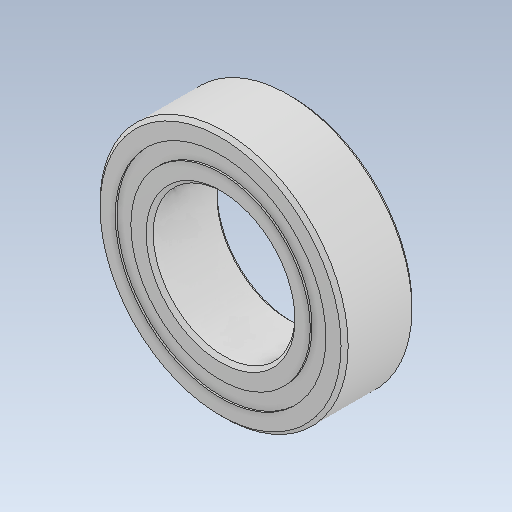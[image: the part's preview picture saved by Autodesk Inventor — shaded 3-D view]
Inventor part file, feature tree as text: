
AUTODESK INVENTOR PART (.ipt)
format: ipt  version: 2020 (Build 240168000, 168)  size: 607,232 bytes
history: native  units: in
note: dims shown in document units (in); Inventor stores cm internally (conversion verified against a paired STEP export)
features: other x11, revolve x5
ambient origin geometry x8: Origin, YZ Plane, XZ Plane, XY Plane, X Axis, Y Axis, Z Axis, Center Point
bodies: Solid1 (feature_tree), Solid2 (feature_tree), Solid3 (feature_tree), Solid4 (feature_tree), Solid5 (feature_tree), Solid6 (feature_tree), Solid7 (feature_tree), Solid8 (feature_tree), Solid9 (feature_tree), Solid10 (feature_tree), Solid11 (feature_tree), Solid12 (feature_tree), Solid13 (feature_tree), Solid14 (feature_tree), Solid15 (feature_tree), Solid16 (feature_tree)
feature tree (16):
  revolve  "Revolve1"  [1 undecoded]
  revolve  "Revolve3"  [1 undecoded]
  revolve  "Revolve4"  [1 undecoded]
  other  "CirPattern1[1]"
  other  "CirPattern1[2]"
  other  "CirPattern1[3]"
  other  "CirPattern1[4]"
  other  "CirPattern1[5]"
  other  "CirPattern1[6]"
  other  "CirPattern1[7]"
  other  "CirPattern1[8]"
  other  "CirPattern1[9]"
  other  "CirPattern1[10]"
  other  "CirPattern1[11]"
  revolve  "Revolve5[1]"  [1 undecoded]
  revolve  "Revolve5[2]"  [1 undecoded]
note: 5 required parameter values undecoded (feature->parameter linkage not recoverable at this tier; creation-order binding heuristic only, values carry confidence <= 0.55)
